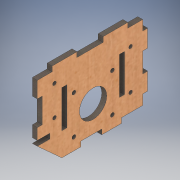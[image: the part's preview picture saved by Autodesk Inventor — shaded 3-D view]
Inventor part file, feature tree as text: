
AUTODESK INVENTOR PART (.ipt)
format: ipt  version: 2019 (Build 230136000, 136)  size: 214,528 bytes
history: native  units: mm
features: sketch x2, other x1, extrude x1, hole x1
ambient origin geometry x8: Origin, YZ Plane, XZ Plane, XY Plane, X Axis, Y Axis, Z Axis, Center Point
bodies: Body1 (feature_tree)
feature tree (5):
  other  "Твердое тело1"
  extrude  "Выдавливание1"  Depth=4.0mm
  hole  "Отверстие1"  [1 undecoded]
  sketch  "Эскиз1"
  sketch  "Эскиз4"
note: 1 required parameter value undecoded (feature->parameter linkage not recoverable at this tier; creation-order binding heuristic only, values carry confidence <= 0.55)
